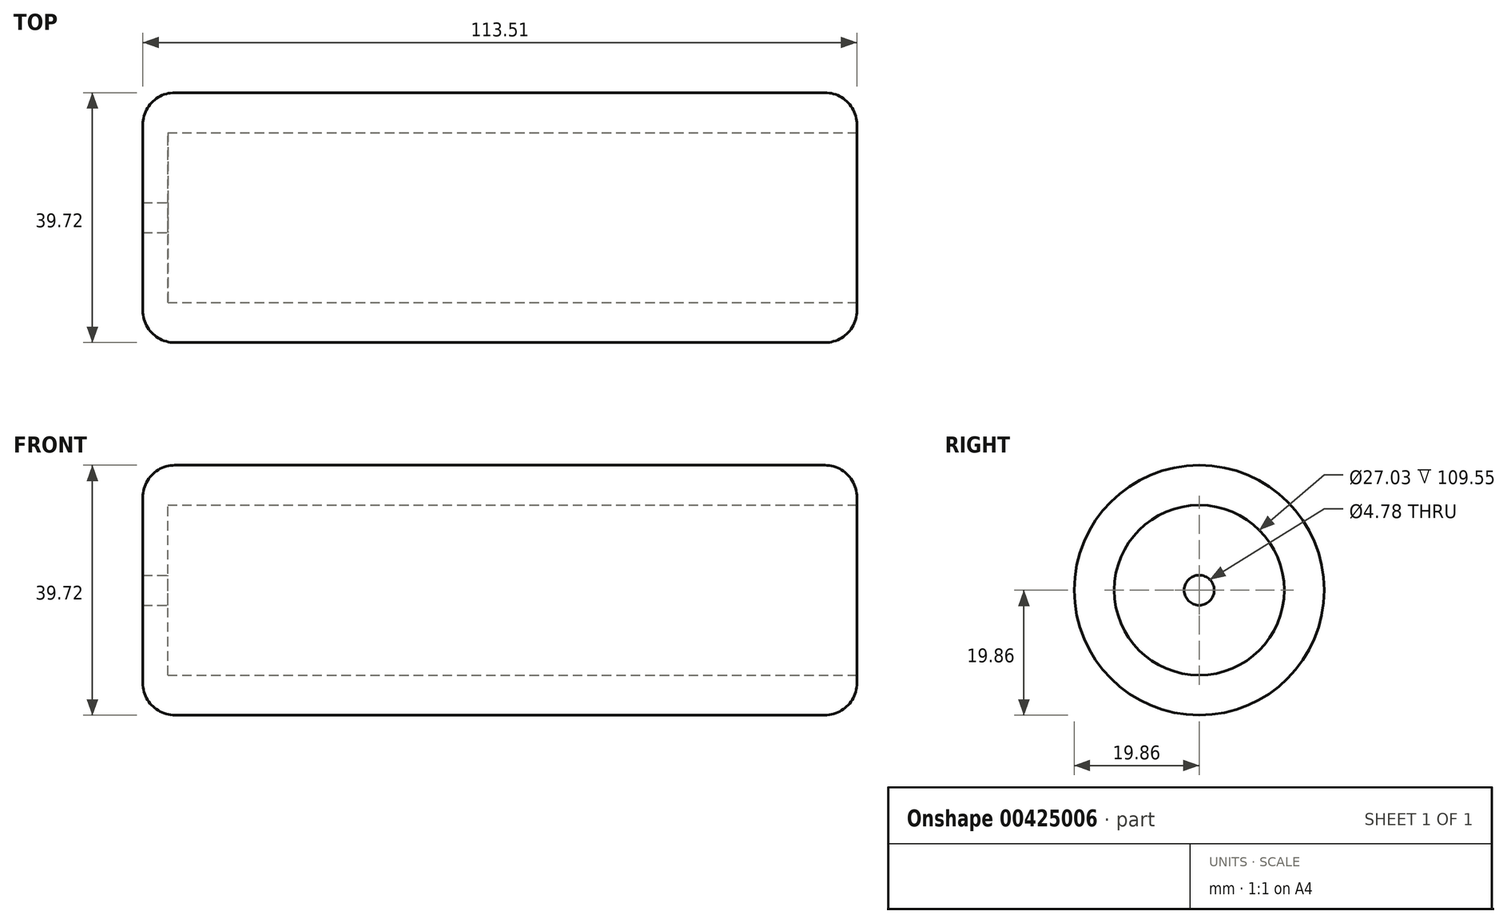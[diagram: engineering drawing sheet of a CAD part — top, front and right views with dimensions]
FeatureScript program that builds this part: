
annotation { "Feature Type Name" : "Feature", "Feature Type Description" : "" }
export const myFeature = defineFeature(function(context is Context, id is Id, definition is map)
    precondition{}
    {
        {
            var Q0;
            Q0=qCreatedBy(makeId("Front.planeOp"),FACE);
            var sketch = newSketch(context, id + "F0", { "sketchPlane" : qUnion([Q0])});
            skLineSegment(sketch, "E0", {"start": v(-46.63, -19.86) * mm, "end": v(66.88, -19.86) * mm});
            skLineSegment(sketch, "E1", {"start": v(66.88, -19.86) * mm, "end": v(66.88, -13.51) * mm});
            skLineSegment(sketch, "E2", {"start": v(-46.63, -19.86) * mm, "end": v(-46.63, -2.39) * mm});
            skLineSegment(sketch, "E3", {"start": v(-46.63, -2.39) * mm, "end": v(-42.67, -2.39) * mm});
            skLineSegment(sketch, "E4", {"start": v(-42.67, -2.39) * mm, "end": v(-42.67, -13.51) * mm});
            skLineSegment(sketch, "E5", {"start": v(-42.67, -13.51) * mm, "end": v(66.88, -13.51) * mm});
            skLineSegment(sketch, "E6", {"start": v(0, 0) * mm, "end": v(-56.14, 0) * mm, "construction": true});
            skSolve(sketch);
        }
        {
            var Q0;
            Q0=makeQuery(id+"F0.imprint","IMPRINT",FACE,{"disambiguationData":[TD([[makeQuery(id+"F0.imprint","IMPRINT",EDGE,{"derivedFrom":sQuery(id+"F0.wireOp",EDGE,"E0")}),1.0]])]});
            var Q1;
            Q1=sQuery(id+"F0.wireOp",EDGE,"E6");
            revolve(context, id + "F1", {"entities" : qUnion([Q0]), "axis" : qUnion([Q1]), "revolveType" : RevolveType.FULL});
        }
        {
            var Q0;
            Q0=makeQuery(id+"F1.opRevolve","SWEPT_EDGE",EDGE,{"disambiguationData":[OSD([sQuery(id+"F0.wireOp",EDGE,"E0"),sQuery(id+"F0.wireOp",EDGE,"E1")])]});
            fillet(context, id + "F2", {"entities" : qUnion([Q0]), "radius" : 5.08 * mm, "tangentPropagation" : true, "allowEdgeOverflow" : false});
        }
        {
            var Q0;
            Q0=makeQuery(id+"F1.opRevolve","SWEPT_EDGE",EDGE,{"disambiguationData":[OSD([sQuery(id+"F0.wireOp",EDGE,"E0"),sQuery(id+"F0.wireOp",EDGE,"E2")])]});
            fillet(context, id + "F3", {"entities" : qUnion([Q0]), "radius" : 5.08 * mm, "tangentPropagation" : true, "allowEdgeOverflow" : false});
        }
    });
